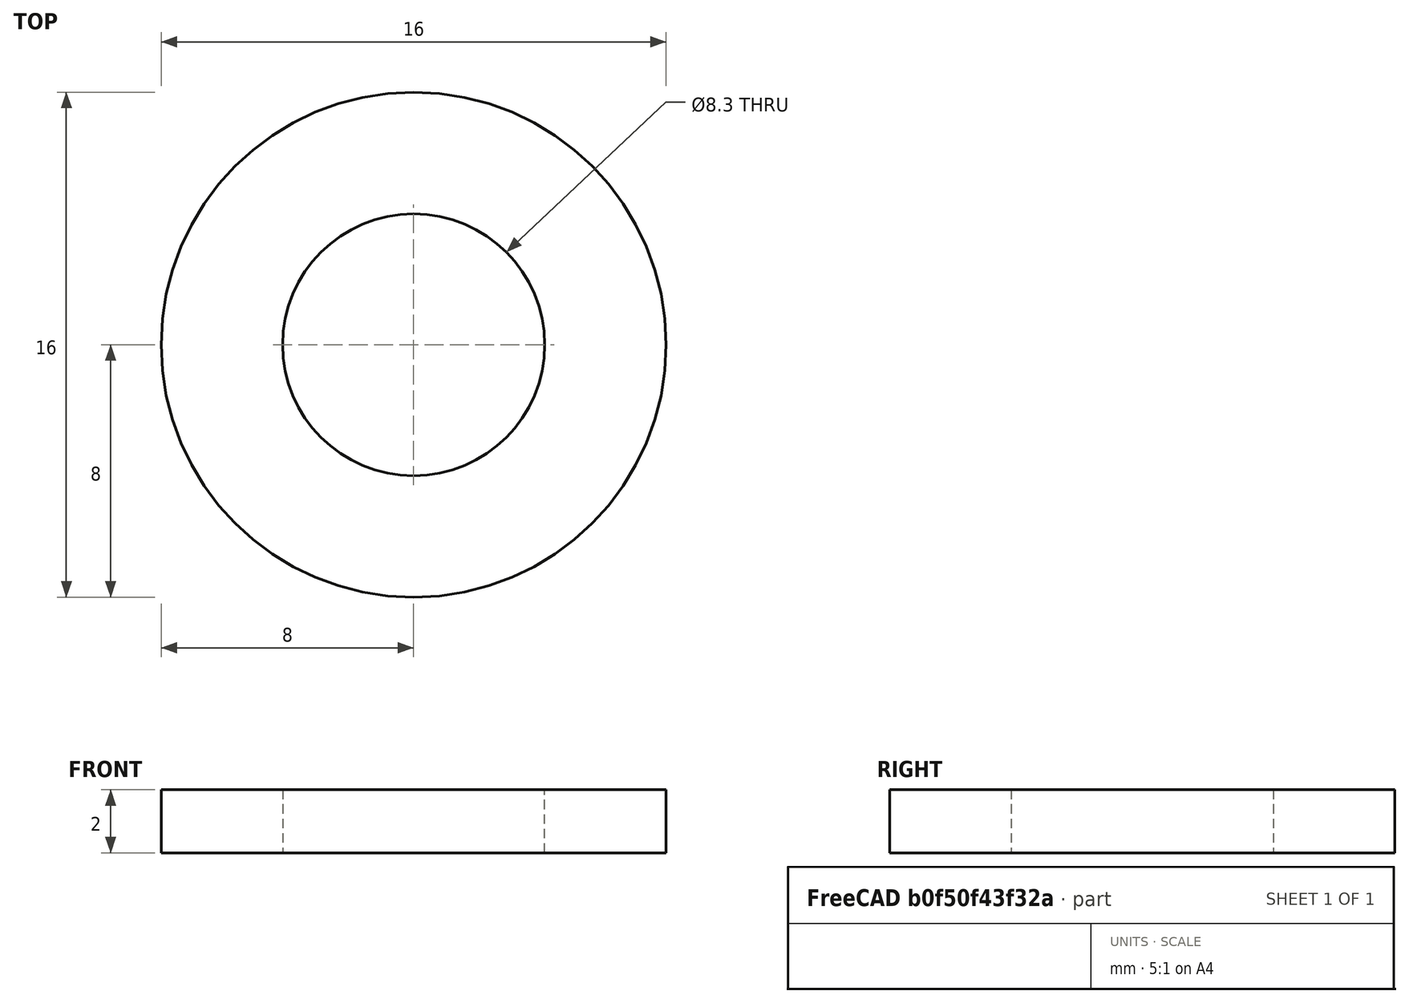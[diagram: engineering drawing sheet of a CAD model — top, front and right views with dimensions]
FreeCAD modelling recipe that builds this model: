
FCSTD DOCUMENT  (FreeCAD 0.19R17089 +1543 (Git))
Label: asm3-basics-3-002
License: All rights reserved
LicenseURL: http://en.wikipedia.org/wiki/All_rights_reserved
objects: Part::FeaturePython×4, App::FeaturePython×2, Sketcher::SketchObject×1, PartDesign::Pad×1, PartDesign::Body×1, App::DocumentObjectGroup×1
note: 7 computed .brp shape members not serialized (recipe doc carries the construction recipe); baked Part::Feature solids carry a one-line shape summary decoded from their .brp

FEATURE [Sketcher::SketchObject] Sketch
  MapMode = 5
  Support = -> [XY_Plane]
  sketch-geometry (2):
    g0: Circle CenterX=0 CenterY=0 CenterZ=0 NormalX=0 NormalY=0 NormalZ=1 AngleXU=0 Radius=4.15
    g1: Circle CenterX=0 CenterY=0 CenterZ=0 NormalX=0 NormalY=0 NormalZ=1 AngleXU=0 Radius=8
  constraints (4):
    c: Coincident(g0,g-1)
    c: Coincident(g1,g0)
    c: Diameter(g0) = 8.3  'D1'
    c: Diameter(g1) = 16  'D2'
FEATURE [PartDesign::Pad] Pad
  ClaimChildren = false
  Length = 2
  Length2 = 100
  Profile = -> Sketch
  Type = 0
FEATURE [PartDesign::Body] Body
  Group = -> [Sketch,Pad]
  Origin = -> Origin
  Tip = -> Pad
FEATURE [App::FeaturePython] Constraints  # WARN: FeaturePython — macro-defined, semantics opaque (R4)
  GroupMode = 1
  _Version = 1
FEATURE [Part::FeaturePython] Parts  # WARN: FeaturePython — macro-defined, semantics opaque (R4)
  Group = -> [Body]
  GroupMode = 0
FEATURE [App::DocumentObjectGroup] Group  label="Repository"
  Group = -> [Assembly]
FEATURE [Part::FeaturePython] Assembly  label="Assembly000 000"  # WARN: FeaturePython — macro-defined, semantics opaque (R4)
  AutoRelax = true
  BuildShape = 0
  Freeze = false
  Group = -> [Constraints,Elements,Parts]
  GroupMode = 1
  SolverType = 1
  Verbose = false
  _SolverType = 1
  _Version = 1
FEATURE [App::FeaturePython] Elements  # WARN: FeaturePython — macro-defined, semantics opaque (R4)
  Group = -> [Element,Element001]
  GroupMode = 1
FEATURE [Part::FeaturePython] Element  # link proxy (typed FeaturePython)
  Detach = false
  LinkTransform = true
  LinkedObject = -> Body [Pad.Edge5]
  _Parent = -> Elements
FEATURE [Part::FeaturePython] Element001  # link proxy (typed FeaturePython)
  Detach = false
  LinkTransform = true
  LinkedObject = -> Body [Pad.Edge6]
  _Parent = -> Elements
